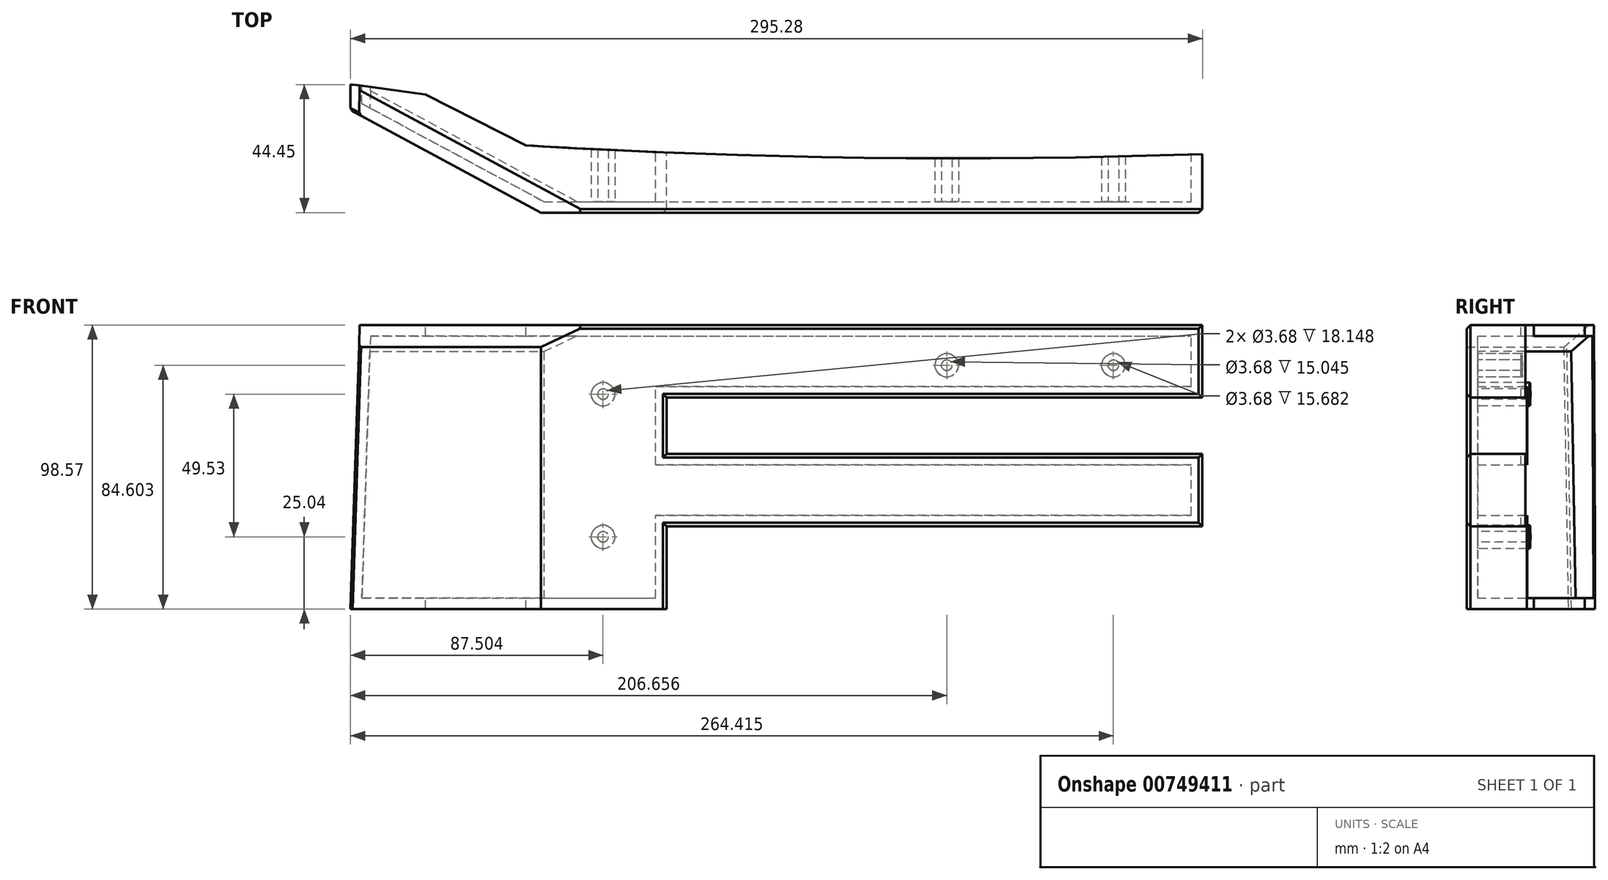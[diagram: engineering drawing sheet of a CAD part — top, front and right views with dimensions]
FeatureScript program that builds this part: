
annotation { "Feature Type Name" : "Feature", "Feature Type Description" : "" }
export const myFeature = defineFeature(function(context is Context, id is Id, definition is map)
    precondition{}
    {
        {
            var Q0;
            Q0=qCreatedBy(makeId("Front.planeOp"),FACE);
            var sketch = newSketch(context, id + "F0", { "sketchPlane" : qUnion([Q0])});
            skLineSegment(sketch, "E0", {"start": v(-93.71, 28.61) * mm, "end": v(-96.89, -69.96) * mm});
            skLineSegment(sketch, "E1", {"start": v(198.39, 28.61) * mm, "end": v(198.39, 3.47) * mm});
            skLineSegment(sketch, "E2", {"start": v(198.39, 3.47) * mm, "end": v(12.71, 3.47) * mm});
            skLineSegment(sketch, "E3", {"start": v(12.71, 3.47) * mm, "end": v(12.71, -16.1) * mm});
            skLineSegment(sketch, "E4", {"start": v(12.71, -16.1) * mm, "end": v(198.39, -16.1) * mm});
            skLineSegment(sketch, "E5", {"start": v(198.39, -16.1) * mm, "end": v(198.39, -41.24) * mm});
            skLineSegment(sketch, "E6", {"start": v(198.39, -41.24) * mm, "end": v(12.71, -41.24) * mm});
            skLineSegment(sketch, "E7", {"start": v(12.71, -41.24) * mm, "end": v(12.71, -69.96) * mm});
            skLineSegment(sketch, "E8", {"start": v(-93.71, 28.61) * mm, "end": v(-27.67, 28.61) * mm});
            skLineSegment(sketch, "E9", {"start": v(-27.67, 28.61) * mm, "end": v(198.39, 28.61) * mm});
            skLineSegment(sketch, "E10", {"start": v(-96.89, -69.96) * mm, "end": v(-17.51, -69.96) * mm});
            skLineSegment(sketch, "E11", {"start": v(-17.51, -69.96) * mm, "end": v(12.71, -69.96) * mm});
            skSolve(sketch);
        }
        {
            var Q0;
            Q0 = qSketchRegion(id + "F0", true);
            extrude(context, id + "F1", {"entities" : qUnion([Q0]), "depth" : 44.45 * mm, "offsetDistance" : 25.4 * mm});
        }
        {
            var Q0;
            Q0=makeQuery(id+"F1.opExtrude","SWEPT_FACE",FACE,{"disambiguationData":[OSD([sQuery(id+"F0.wireOp",EDGE,"E10"),sQuery(id+"F0.wireOp",EDGE,"E11")])]});
            var sketch = newSketch(context, id + "F2", { "sketchPlane" : qUnion([Q0])});
            skLineSegment(sketch, "E12", {"start": v(-96.89, 8.89) * mm, "end": v(-96.89, 44.45) * mm});
            skLineSegment(sketch, "E13", {"start": v(-96.89, 44.45) * mm, "end": v(-30.85, 44.45) * mm});
            skLineSegment(sketch, "E14", {"start": v(-30.85, 44.45) * mm, "end": v(-96.89, 8.89) * mm});
            skSolve(sketch);
        }
        {
            var Q0;
            Q0=makeQuery(id+"F1.opExtrude","SWEPT_FACE",FACE,{"disambiguationData":[OSD([sQuery(id+"F0.wireOp",EDGE,"E6")])]});
            var sketch = newSketch(context, id + "F3", { "sketchPlane" : qUnion([Q0])});
            skLineSegment(sketch, "E15", {"start": v(-96.13, 0) * mm, "end": v(-70.97, 3.5) * mm});
            skLineSegment(sketch, "E16", {"start": v(-70.97, 3.5) * mm, "end": v(-36.06, 21.13) * mm});
            skArc(sketch, "E17", {"start": v(198.39, 24.13) * mm, "mid": v(81.13, 25.4) * mm, "end": v(-36.06, 21.13) * mm});
            skLineSegment(sketch, "E18", {"start": v(198.39, 24.13) * mm, "end": v(198.39, 0) * mm});
            skLineSegment(sketch, "E19", {"start": v(198.39, 0) * mm, "end": v(-96.13, 0) * mm});
            skSolve(sketch);
        }
        {
            var Q0;
            Q0 = qSketchRegion(id + "F2", true);
            extrude(context, id + "F4", {"entities" : qUnion([Q0]), "operationType" : NewBodyOperationType.REMOVE, "endBound" : BoundingType.THROUGH_ALL, "oppositeDirection" : true, "depth" : 25.4 * mm, "offsetDistance" : 25.4 * mm});
        }
        {
            var Q0;
            Q0=makeQuery(id+"F4.boolean.opBoolean","INTERSECT",EDGE,{"derivedFrom":[makeQuery(id+"F1.opExtrude","SWEPT_FACE",FACE,{"disambiguationData":[OSD([sQuery(id+"F0.wireOp",EDGE,"E8"),sQuery(id+"F0.wireOp",EDGE,"E9")])]}),makeQuery(id+"F4.opExtrude","SWEPT_FACE",FACE,{"disambiguationData":[OSD([sQuery(id+"F2.wireOp",EDGE,"E14")])]})]});
            chamfer(context, id + "F5", {"entities" : qUnion([Q0]), "width" : 7.62 * mm, "tangentPropagation" : true});
        }
        {
            var Q0;
            Q0=makeQuery(id+"F1.opExtrude","CAP_EDGE",EDGE,{"disambiguationData":[OSD([sQuery(id+"F0.wireOp",EDGE,"E8"),sQuery(id+"F0.wireOp",EDGE,"E9")])],"isStart":false});
            var Q1;
            Q1=makeQuery(id+"F1.opExtrude","CAP_EDGE",EDGE,{"disambiguationData":[OSD([sQuery(id+"F0.wireOp",EDGE,"E1")])],"isStart":false});
            var Q2;
            Q2=makeQuery(id+"F1.opExtrude","CAP_EDGE",EDGE,{"disambiguationData":[OSD([sQuery(id+"F0.wireOp",EDGE,"E2")])],"isStart":false});
            var Q3;
            Q3=makeQuery(id+"F1.opExtrude","CAP_EDGE",EDGE,{"disambiguationData":[OSD([sQuery(id+"F0.wireOp",EDGE,"E4")])],"isStart":false});
            var Q4;
            Q4=makeQuery(id+"F1.opExtrude","CAP_EDGE",EDGE,{"disambiguationData":[OSD([sQuery(id+"F0.wireOp",EDGE,"E6")])],"isStart":false});
            var Q5;
            Q5=makeQuery(id+"F1.opExtrude","CAP_EDGE",EDGE,{"disambiguationData":[OSD([sQuery(id+"F0.wireOp",EDGE,"E5")])],"isStart":false});
            var Q6;
            Q6=makeQuery(id+"F1.opExtrude","CAP_EDGE",EDGE,{"disambiguationData":[OSD([sQuery(id+"F0.wireOp",EDGE,"E7")])],"isStart":false});
            var Q7;
            Q7=makeQuery(id+"F1.opExtrude","CAP_EDGE",EDGE,{"disambiguationData":[OSD([sQuery(id+"F0.wireOp",EDGE,"E3")])],"isStart":false});
            var Q8;
            Q8=makeQuery(id+"F4.boolean.opBoolean","INTERSECT",EDGE,{"derivedFrom":[makeQuery(id+"F1.opExtrude","SWEPT_FACE",FACE,{"disambiguationData":[OSD([sQuery(id+"F0.wireOp",EDGE,"E0")])]}),makeQuery(id+"F4.opExtrude","SWEPT_FACE",FACE,{"disambiguationData":[OSD([sQuery(id+"F2.wireOp",EDGE,"E14")])]})]});
            chamfer(context, id + "F6", {"entities" : qUnion([Q0, Q1, Q2, Q3, Q4, Q5, Q6, Q7, Q8]), "width" : 1.27 * mm, "tangentPropagation" : true});
        }
        {
            var Q0;
            Q0=makeQuery(id+"F1.opExtrude","CAP_FACE",FACE,{"disambiguationData":[OSD([sQuery(id+"F0.wireOp",EDGE,"E0"),sQuery(id+"F0.wireOp",EDGE,"E1"),sQuery(id+"F0.wireOp",EDGE,"E2"),sQuery(id+"F0.wireOp",EDGE,"E3"),sQuery(id+"F0.wireOp",EDGE,"E4"),sQuery(id+"F0.wireOp",EDGE,"E5"),sQuery(id+"F0.wireOp",EDGE,"E6"),sQuery(id+"F0.wireOp",EDGE,"E7"),sQuery(id+"F0.wireOp",EDGE,"E8"),sQuery(id+"F0.wireOp",EDGE,"E9"),sQuery(id+"F0.wireOp",EDGE,"E10"),sQuery(id+"F0.wireOp",EDGE,"E11")])],"isStart":true});
            shell(context, id + "F7", {"entities" : qUnion([Q0]), "thickness" : 3.8 * mm});
        }
        {
            var Q0;
            Q0=makeQuery(id+"F7.opShell","OFFSET_FACE",FACE,{"disambiguationData":[OSD([sQuery(id+"F0.wireOp",EDGE,"E0"),sQuery(id+"F0.wireOp",EDGE,"E1"),sQuery(id+"F0.wireOp",EDGE,"E2"),sQuery(id+"F0.wireOp",EDGE,"E3"),sQuery(id+"F0.wireOp",EDGE,"E4"),sQuery(id+"F0.wireOp",EDGE,"E5"),sQuery(id+"F0.wireOp",EDGE,"E6"),sQuery(id+"F0.wireOp",EDGE,"E7"),sQuery(id+"F0.wireOp",EDGE,"E8"),sQuery(id+"F0.wireOp",EDGE,"E9"),sQuery(id+"F0.wireOp",EDGE,"E10"),sQuery(id+"F0.wireOp",EDGE,"E11")])]});
            var sketch = newSketch(context, id + "F8", { "sketchPlane" : qUnion([Q0])});
            skCircle(sketch, "E20", {"center": v(-167.53, 14.64) * mm, "radius": 4.09 * mm});
            skCircle(sketch, "E21", {"center": v(-167.53, 14.64) * mm, "radius": 1.84 * mm});
            skCircle(sketch, "E22", {"center": v(-109.77, 14.64) * mm, "radius": 4.09 * mm});
            skCircle(sketch, "E23", {"center": v(-109.77, 14.64) * mm, "radius": 1.84 * mm});
            skCircle(sketch, "E24", {"center": v(9.39, -44.92) * mm, "radius": 4.09 * mm});
            skCircle(sketch, "E25", {"center": v(9.39, -44.92) * mm, "radius": 1.84 * mm});
            skCircle(sketch, "E26", {"center": v(9.39, 4.6) * mm, "radius": 4.09 * mm});
            skCircle(sketch, "E27", {"center": v(9.39, 4.6) * mm, "radius": 1.84 * mm});
            skSolve(sketch);
        }
        {
            var Q0;
            Q0 = qSketchRegion(id + "F8", true);
            var Q1;
            Q1=makeQuery(id+"F1.opExtrude","CAP_FACE",FACE,{"disambiguationData":[OSD([sQuery(id+"F0.wireOp",EDGE,"E0"),sQuery(id+"F0.wireOp",EDGE,"E1"),sQuery(id+"F0.wireOp",EDGE,"E2"),sQuery(id+"F0.wireOp",EDGE,"E3"),sQuery(id+"F0.wireOp",EDGE,"E4"),sQuery(id+"F0.wireOp",EDGE,"E5"),sQuery(id+"F0.wireOp",EDGE,"E6"),sQuery(id+"F0.wireOp",EDGE,"E7"),sQuery(id+"F0.wireOp",EDGE,"E8"),sQuery(id+"F0.wireOp",EDGE,"E9"),sQuery(id+"F0.wireOp",EDGE,"E10"),sQuery(id+"F0.wireOp",EDGE,"E11")])],"isStart":true});
            extrude(context, id + "F9", {"entities" : qUnion([Q0]), "operationType" : NewBodyOperationType.ADD, "endBound" : BoundingType.UP_TO_SURFACE, "depth" : 25.4 * mm, "endBoundEntityFace" : qUnion([Q1]), "offsetDistance" : 25.4 * mm});
        }
        {
            var Q0;
            Q0 = qSketchRegion(id + "F3", true);
            extrude(context, id + "F10", {"entities" : qUnion([Q0]), "operationType" : NewBodyOperationType.REMOVE, "endBound" : BoundingType.SYMMETRIC, "depth" : 254 * mm, "offsetDistance" : 25.4 * mm});
        }
    });
